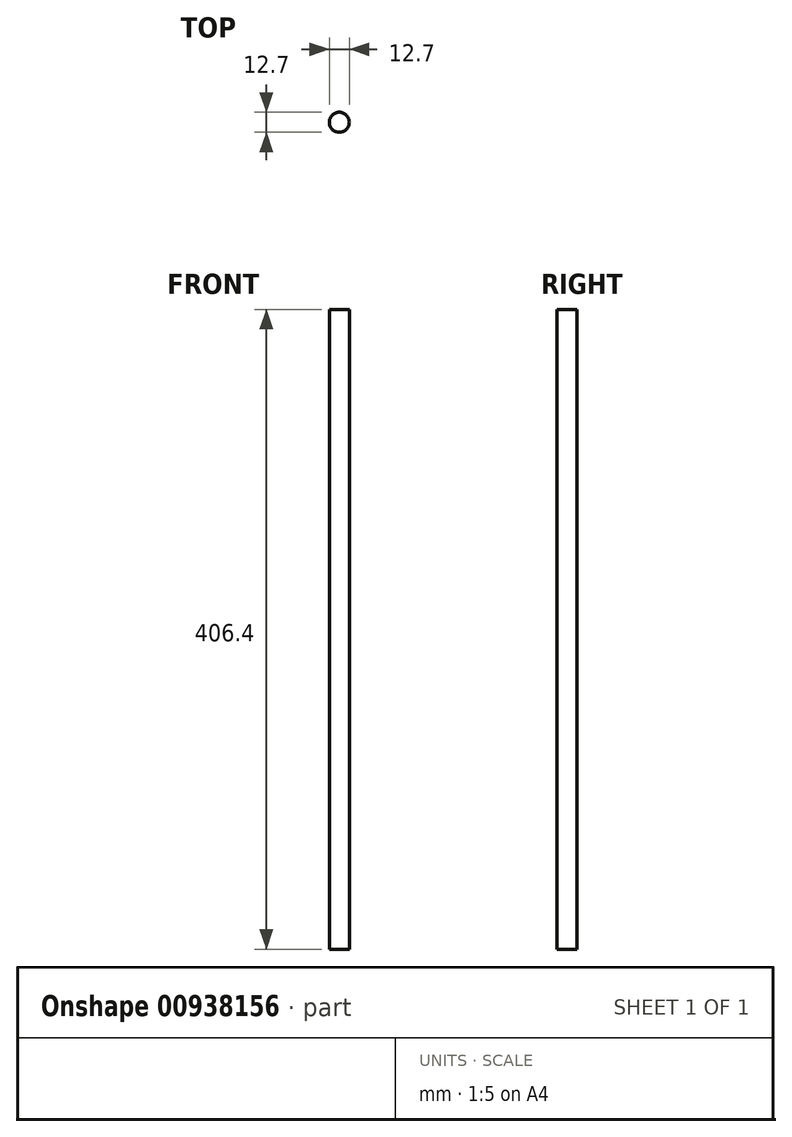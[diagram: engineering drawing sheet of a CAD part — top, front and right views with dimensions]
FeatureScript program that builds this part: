
annotation { "Feature Type Name" : "Feature", "Feature Type Description" : "" }
export const myFeature = defineFeature(function(context is Context, id is Id, definition is map)
    precondition{}
    {
        {
            var Q0;
            Q0=qCreatedBy(makeId("Top.planeOp"),FACE);
            var sketch = newSketch(context, id + "F0", { "sketchPlane" : qUnion([Q0])});
            skCircle(sketch, "E0", {"center": v(-56.28, 41.87) * mm, "radius": 6.35 * mm});
            skSolve(sketch);
        }
        {
            var Q0;
            Q0=makeQuery(id+"F0.imprint","IMPRINT",FACE,{"disambiguationData":[TD([[makeQuery(id+"F0.imprint","IMPRINT",EDGE,{"derivedFrom":sQuery(id+"F0.wireOp",EDGE,"E0")}),1.0]])]});
            extrude(context, id + "F1", {"entities" : qUnion([Q0]), "depth" : 406.4 * mm, "offsetDistance" : 25 * mm});
        }
    });
